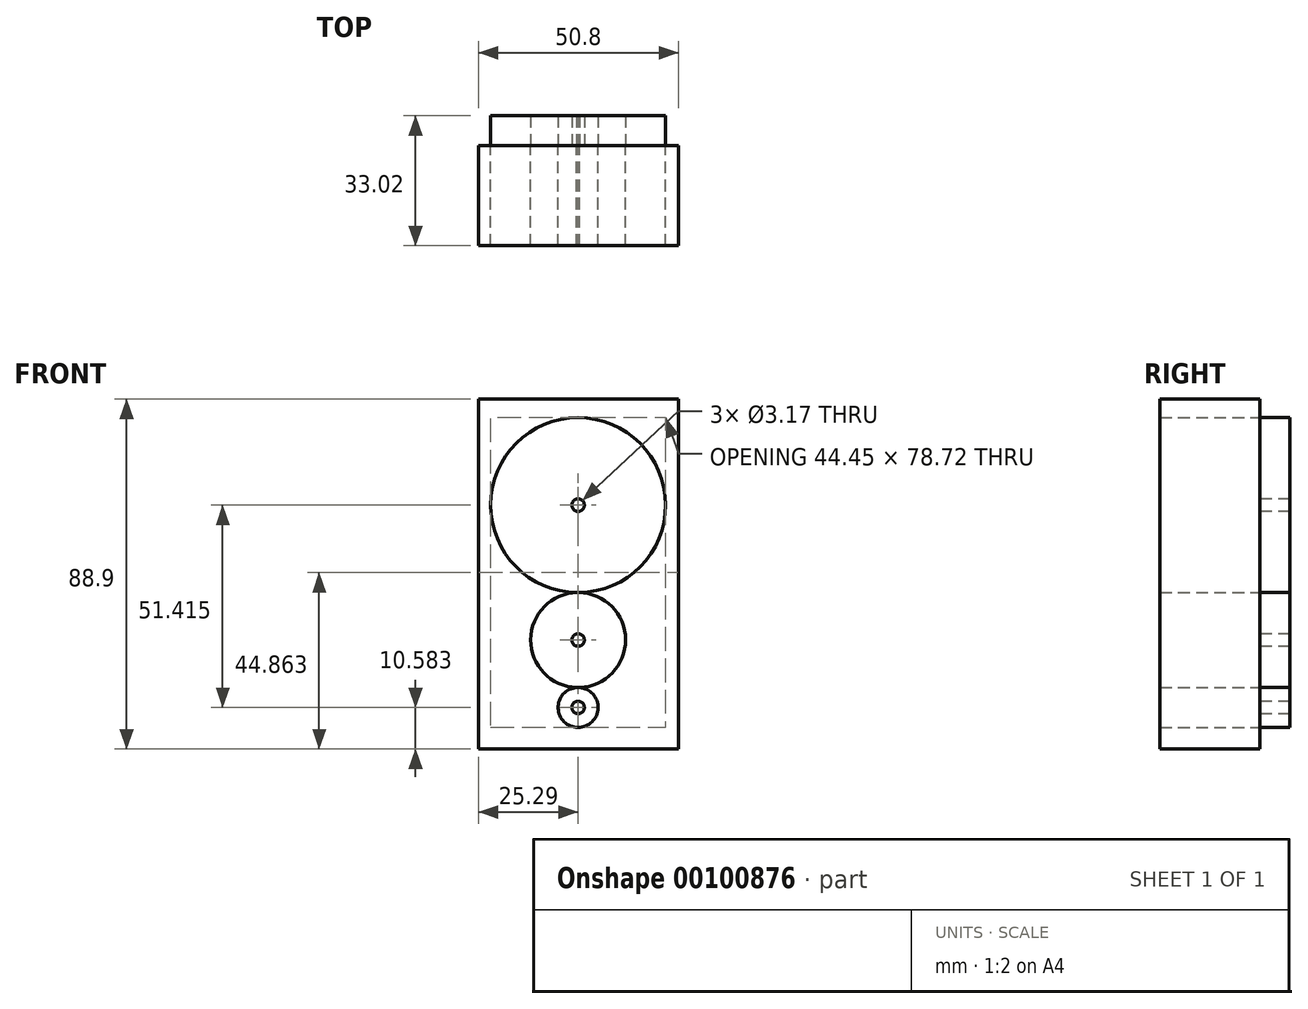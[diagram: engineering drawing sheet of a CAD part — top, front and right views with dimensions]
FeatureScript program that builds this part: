
annotation { "Feature Type Name" : "Feature", "Feature Type Description" : "" }
export const myFeature = defineFeature(function(context is Context, id is Id, definition is map)
    precondition{}
    {
        {
            var Q0;
            Q0=qCreatedBy(makeId("Front.planeOp"),FACE);
            var sketch = newSketch(context, id + "F0", { "sketchPlane" : qUnion([Q0])});
            skLineSegment(sketch, "E0.bottom", {"start": v(-25.29, 75.37) * mm, "end": v(25.51, 75.37) * mm});
            skLineSegment(sketch, "E0.top", {"start": v(-25.29, -13.53) * mm, "end": v(25.51, -13.53) * mm});
            skLineSegment(sketch, "E0.left", {"start": v(-25.29, 75.37) * mm, "end": v(-25.29, -13.53) * mm});
            skLineSegment(sketch, "E0.right", {"start": v(25.51, 75.37) * mm, "end": v(25.51, -13.53) * mm});
            skCircle(sketch, "E1", {"center": v(0, 48.47) * mm, "radius": 22.23 * mm});
            skCircle(sketch, "E2", {"center": v(0, 14.18) * mm, "radius": 12.07 * mm});
            skCircle(sketch, "E3", {"center": v(0, 48.47) * mm, "radius": 1.59 * mm});
            skCircle(sketch, "E4", {"center": v(0, 14.18) * mm, "radius": 1.59 * mm});
            skCircle(sketch, "E5", {"center": v(0, -2.95) * mm, "radius": 5.08 * mm});
            skCircle(sketch, "E6", {"center": v(0, -2.95) * mm, "radius": 1.59 * mm});
            skSolve(sketch);
        }
        {
            var Q0;
            Q0=makeQuery(id+"F0.imprint","IMPRINT",FACE,{"disambiguationData":[TD([[makeQuery(id+"F0.imprint","IMPRINT",EDGE,{"derivedFrom":sQuery(id+"F0.wireOp",EDGE,"E0.bottom")}),-1.0]])]});
            extrude(context, id + "F1", {"entities" : qUnion([Q0]), "depth" : 25.4 * mm});
        }
        {
            var Q0;
            Q0=makeQuery(id+"F0.imprint","IMPRINT",FACE,{"disambiguationData":[TD([[makeQuery(id+"F0.imprint","IMPRINT",EDGE,{"derivedFrom":sQuery(id+"F0.wireOp",EDGE,"E3")}),-1.0]])]});
            extrude(context, id + "F2", {"entities" : qUnion([Q0]), "oppositeDirection" : true, "depth" : 7.62 * mm});
        }
        {
            var Q0;
            Q0=makeQuery(id+"F0.imprint","IMPRINT",FACE,{"disambiguationData":[TD([[makeQuery(id+"F0.imprint","IMPRINT",EDGE,{"derivedFrom":sQuery(id+"F0.wireOp",EDGE,"E4")}),-1.0]])]});
            extrude(context, id + "F3", {"entities" : qUnion([Q0]), "oppositeDirection" : true, "depth" : 7.62 * mm});
        }
        {
            var Q0;
            Q0=makeQuery(id+"F0.imprint","IMPRINT",FACE,{"disambiguationData":[TD([[makeQuery(id+"F0.imprint","IMPRINT",EDGE,{"derivedFrom":sQuery(id+"F0.wireOp",EDGE,"E6")}),-1.0]])]});
            extrude(context, id + "F4", {"entities" : qUnion([Q0]), "oppositeDirection" : true, "depth" : 7.62 * mm});
        }
    });
